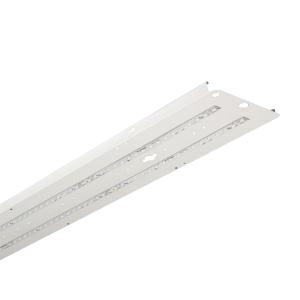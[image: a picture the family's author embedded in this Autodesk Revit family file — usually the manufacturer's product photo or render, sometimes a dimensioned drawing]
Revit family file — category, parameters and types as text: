
# Revit family: 3f_filippi_-_kit_led_retrofit_per_schermo_in_vetro_3f_filippi_-_a5104_-_kit_led_i3f_76__a3f_91__a3f_93-l_7968c7b21b219225
name_source: partatom
category: Lighting Fixtures
units: mm (PartAtom-declared; Revit-internal decimal feet)

## family parameters
Cut with Voids When Loaded = No
Host = Face
Light Source = No
Part Type = Normal
Room Calculation Point = No
Round Connector Dimension = Use Diameter
Shared = No

## types (1)
- 3F Filippi - Kit LED Retrofit per schermo in vetro (1 x LED, 7525 lm, 49 W, 4000 K)
    Apparent Load = 49 VA
    Approval mark = ENEC
    CIE Flux Codes = 59 91 99 100 100
    Color Rendering = 80
    Color Temperature = 4000 K
    Control Gear = Electronic ballast
    Default Elevation = 1800 mm
    Description = Led retrofit kit suitable for Fluorescent Beta 2x i3F 76, A3F 91 and A3F 93 luminaires.

ILLUMINOTECHNICAL
Luminous efficiency 100% (DLOR 97%, ULOR 3%).
Initial luminous flux of the luminaire 7525 lm.
Symmetric concentrated distribution.
Installation Interdistance Transv.D = 0.74 x hu - Long.D = 1.25 x hu.
Tabular UGR (CIE 117 - 4H-8H; S=0.25H; 70/50/20): RUG 17.5 - 23.2.
Beam angle: 65° - 109°.
Luminous efficacy 154 lm/W.
Lifetime (L93/B10): 30000 h. (tq+25°C)
Lifetime (L90/B10): 50000 h. (tq+25°C)
Lifetime (L85/B10): 80000 h. (tq+25°C)
Lifetime (L80/B10): 100000 h. (tq+25°C)
Lifetime (L85/B10): 50000 h. (tq+35°C)
Sudden decreased luminous flux after 50000 hours: 0% (C0).
Photobiological safety in compliance with IEC/TR 62778: RG0 risk exempt, (IEC 62471).
In compliance with IEC/EN 62722-2-1 - IEC/EN 62717 standards.

SOURCE
2 linear LED modules 22W/840.
Energy efficiency class (UE 2019/2020 - UE 2019/2015): D.
CIE 13.3 Colour rendering index: CRI >80 (R9 <50%).
IES TM-30 Fidelity Index: Rf = 84 Rg = 95.
CCT nominal colour temperature 4000 K.
Colour initial tolerance (MacAdam): SDCM 3.

MECHANICAL
Concentrated flow recuperator, oversized, in specular aluminium with superficial titanium-magnesium treatment, non-iridescent.
Gear-tray unit in hot-galvanised steel, painted in white polyester, fixed to the housing by means of "Ribloc" rapid devices in galvanised steel, hinged opening.
Luminaire with limited surface temperature. - D - (EN 60598-2-24)
Dimensions: 1565x235 mm, height 135 mm. Weight 2.11 kg.
Glow-wire test resistance 850°C.

ELECTRICAL
Halogen Free electronic wiring 230V-50/60Hz, power factor 0.97, THD <25%, constant output current, SELV, class I, 1 driver.
Power of the luminaire 49 W.
CE - IEC 60598-1 - EN 60598-1.
SAFE FLICKER: PstLM=<1 and SVM=<0.4 (IEC TR 61547-1 and IEC TR 63158), to ensure a more comfortable and safe light.
Luminaire compliant with EN 60598-2-22 for power supply from a centralised emergency system CPSS (Central Power Supply System), not incorporated in the luminaire - high risk areas excluded. The default power and flux are 100% in AC and 100% in DC.
Ambient temperature from -20°C to +35°C.
Temperature class T6 max 85°C.
Relative humidity UR: <85%.

INSTALLATION
Retrofit.
Correct installation of the retrofit LED kit, compliant with EN 60598-1 and CE marked, inside the 3F Filippi - Beta 2x i3F 76, A3F 91 and A3F 93 Fluorescent luminaires must be only carried out by qualified personnel to ensure compliance with the national installation standards.
Attention: to maintain the degree of protection of the device and for the purposes of validity of the guarantee of the new retrofit kits, it is imperative to replace the old cable guides (on the body of the device) with the new ones supplied.
All accessories dedicated to this product are available on the Catalog and on our website www.3F-Filippi.com.

WARNING
Fixture not suitable for cold stores with an ambient temperature <0°C and/or relative humidity >85%.
Luminaire designed for disposal/recycling at end-of-life.
Replaceable (LED only) light source by a professional. Replaceable control gear by a professional.
    Height = 135 mm
    Lamp = 1 x LED
    Lamp Light Flux = 7525 lm
    Lamp Power = 49 W
    Lamp count = 1
    Length = 1565 mm
    Lifetime = 50000 h
    Luminous efficacy = 154 lm/W
    Manufacturer = 3F Filippi
    ModVariant = No
    Model = 3F Filippi - A5104 - Kit LED I3F 76, A3F 91, A3F 93-L1565-2X22W CONC
    Mounting Place = Ceiling
    Mounting Type = Surface mounted
    Number of Poles = 1
    OnlyDefault = Yes
    Power Factor = 1
    Product Name = 3F Filippi - Kit LED Retrofit per schermo in vetro
    Product group = ceiling mounted luminaire
    ProductGroupID = 3
    Protection Class = Protection class I
    Protection Degree = Degree of protection
    RLX_Detail_Level = 1
    RLX_Emergency_Light_Flux = 0 lm
    RLX_Emergency_Type = 0
    RLX_Emergency_Type_DB = No
    RlxData = <blob elided: 53941 chars, md5=13962d6e>
    Socket = socket
    Standby Power = 0 W
    System Light Flux = 7525 lm
    System Power = 49 W
    Type Comments = Product without accessories
    Type Image = 3ffilippi_a5104.jpg
    URL = http://relux.com
    VarID = ---
    Voltage = 0 V
    Weight = 0.00 kg
    Width = 235 mm

## geometry (parser evidence)
native form markers: Blend x4, Sweep x13
no freeform markers — native parametric forms only
